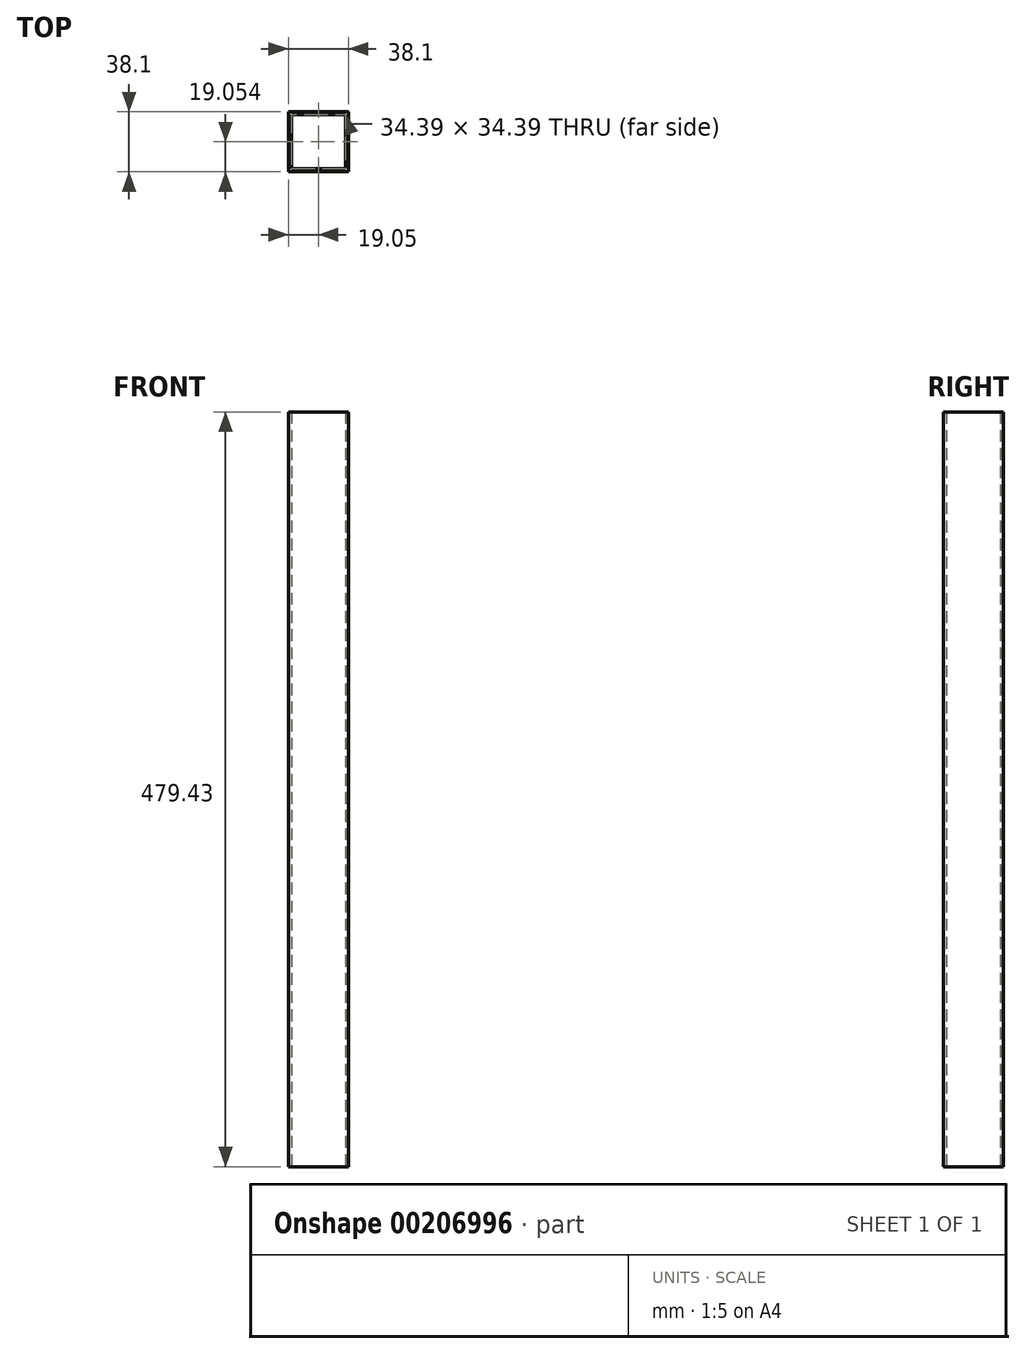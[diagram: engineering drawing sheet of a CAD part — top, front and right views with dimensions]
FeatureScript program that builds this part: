
annotation { "Feature Type Name" : "Feature", "Feature Type Description" : "" }
export const myFeature = defineFeature(function(context is Context, id is Id, definition is map)
    precondition{}
    {
        {
            var Q0;
            Q0=qCreatedBy(makeId("Top.planeOp"),FACE);
            var sketch = newSketch(context, id + "F0", { "sketchPlane" : qUnion([Q0])});
            skLineSegment(sketch, "E0.bottom", {"start": v(-66.32, -59.86) * mm, "end": v(-28.22, -59.86) * mm});
            skLineSegment(sketch, "E0.top", {"start": v(-66.32, -21.76) * mm, "end": v(-28.22, -21.76) * mm});
            skLineSegment(sketch, "E0.left", {"start": v(-66.32, -59.86) * mm, "end": v(-66.32, -21.76) * mm});
            skLineSegment(sketch, "E0.right", {"start": v(-28.22, -59.86) * mm, "end": v(-28.22, -21.76) * mm});
            skLineSegment(sketch, "E1.bottom", {"start": v(-64.47, -58) * mm, "end": v(-30.07, -58) * mm});
            skLineSegment(sketch, "E1.top", {"start": v(-64.47, -23.6) * mm, "end": v(-30.07, -23.6) * mm});
            skLineSegment(sketch, "E1.left", {"start": v(-64.47, -58) * mm, "end": v(-64.47, -23.6) * mm});
            skLineSegment(sketch, "E1.right", {"start": v(-30.07, -58) * mm, "end": v(-30.07, -23.6) * mm});
            skSolve(sketch);
        }
        {
            var Q0;
            Q0 = qSketchRegion(id + "F0", true);
            extrude(context, id + "F1", {"entities" : qUnion([Q0]), "depth" : 479.42 * mm});
        }
    });
